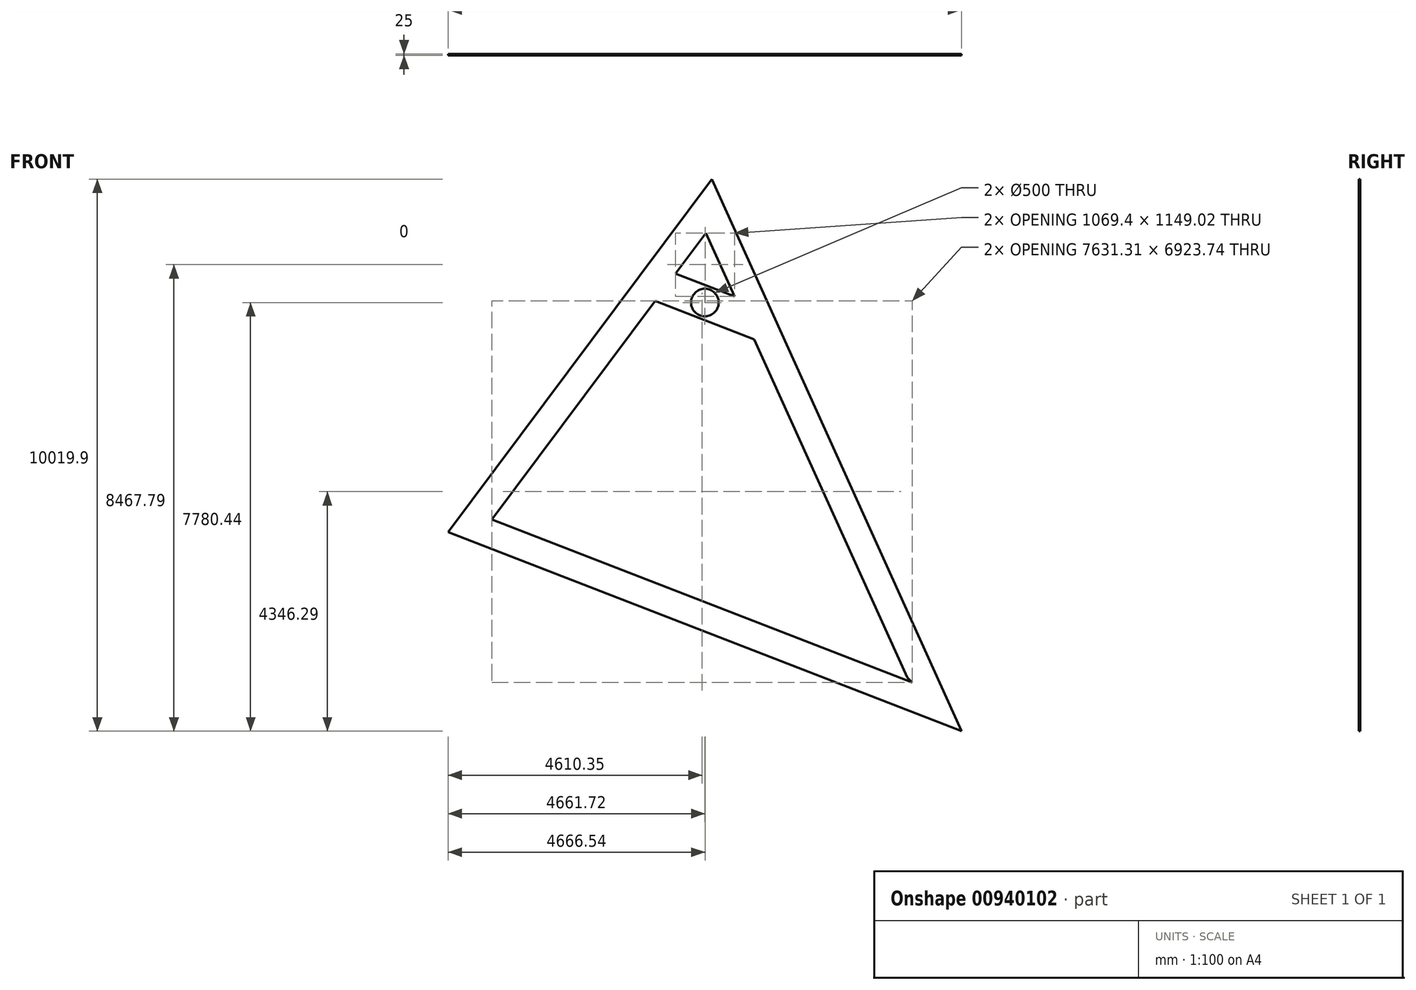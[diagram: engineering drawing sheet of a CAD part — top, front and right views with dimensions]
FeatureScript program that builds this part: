
annotation { "Feature Type Name" : "Feature", "Feature Type Description" : "" }
export const myFeature = defineFeature(function(context is Context, id is Id, definition is map)
    precondition{}
    {
        {
            var Q0;
            Q0=qCreatedBy(makeId("Front.planeOp"),FACE);
            var sketch = newSketch(context, id + "F0", { "sketchPlane" : qUnion([Q0])});
            skLineSegment(sketch, "E0", {"start": v(1258.9, -6409.87) * mm, "end": v(10584.54, -10019.94) * mm});
            skLineSegment(sketch, "E1", {"start": v(10584.54, -10019.94) * mm, "end": v(6045.72, 0) * mm});
            skLineSegment(sketch, "E2", {"start": v(6045.72, 0) * mm, "end": v(1258.9, -6409.87) * mm});
            skLineSegment(sketch, "E3", {"start": v(1258.9, -6409.87) * mm, "end": v(8315.13, -5009.97) * mm});
            skLineSegment(sketch, "E4", {"start": v(10584.54, -10019.94) * mm, "end": v(3652.31, -3204.93) * mm});
            skPoint(sketch, "E5", {"position": v(5963.05, -5476.6) * mm});
            skLineSegment(sketch, "E6", {"start": v(1743, -6597.27) * mm, "end": v(6281.33, -520.13) * mm});
            skLineSegment(sketch, "E7", {"start": v(5704.05, -457.51) * mm, "end": v(9918.91, -9762.26) * mm});
            skLineSegment(sketch, "E8", {"start": v(1569.5, -5993.95) * mm, "end": v(10290.02, -9369.77) * mm});
            skLineSegment(sketch, "E9", {"start": v(5390.74, -1712.68) * mm, "end": v(6460.14, -2126.66) * mm});
            skLineSegment(sketch, "E10", {"start": v(5018.02, -2211.78) * mm, "end": v(6813.56, -2906.86) * mm});
            skCircle(sketch, "E11", {"center": v(5920.62, -2239.5) * mm, "radius": 250 * mm});
            skPoint(sketch, "E12", {"position": v(5915.79, -2559.32) * mm});
            skPoint(sketch, "E13", {"position": v(5925.44, -1919.67) * mm});
            skLineSegment(sketch, "E14", {"start": v(5925.44, -1919.67) * mm, "end": v(5915.79, -2559.32) * mm});
            skSolve(sketch);
        }
        {
            var Q0;
            {var subQ1=sQuery(id+"F0.wireOp",EDGE,"E2");var subQ6=sQuery(id+"F0.wireOp",EDGE,"E4");var subQ9=makeQuery(id+"F0.imprint","INTERSECT",VERTEX,{"derivedFrom":[subQ1,subQ6]});Q0=makeQuery(id+"F0.imprint","IMPRINT",FACE,{"disambiguationData":[TD([[makeQuery(id+"F0.imprint","IMPRINT",EDGE,{"disambiguationData":[TD([[subQ9,1.0]])],"derivedFrom":subQ1}),1.0]])]});}
            var Q1;
            {var subQ0=sQuery(id+"F0.wireOp",EDGE,"fM5ZJTd4-uyG9-POUc-NQYo-ETeNcUDX0p3K");var subQ1=sQuery(id+"F0.wireOp",EDGE,"E6");var subQ2=makeQuery(id+"F0.imprint","INTERSECT",VERTEX,{"derivedFrom":[subQ1,subQ0]});Q1=makeQuery(id+"F0.imprint","IMPRINT",FACE,{"disambiguationData":[TD([[makeQuery(id+"F0.imprint","IMPRINT",EDGE,{"disambiguationData":[TD([[subQ2,-1.0]])],"derivedFrom":subQ1}),1.0]])]});}
            var Q2;
            {var subQ1=sQuery(id+"F0.wireOp",EDGE,"E2");var subQ3=sQuery(id+"F0.wireOp",EDGE,"E7");var subQ4=makeQuery(id+"F0.imprint","INTERSECT",VERTEX,{"derivedFrom":[subQ1,subQ3]});Q2=makeQuery(id+"F0.imprint","IMPRINT",FACE,{"disambiguationData":[TD([[makeQuery(id+"F0.imprint","IMPRINT",EDGE,{"disambiguationData":[TD([[subQ4,-1.0]])],"derivedFrom":subQ3}),1.0]])]});}
            var Q3;
            {var subQ1=sQuery(id+"F0.wireOp",EDGE,"c8Q3rwKz-DZUh-2BjS-u902-BvDDxR5sp2cA");var subQ3=sQuery(id+"F0.wireOp",EDGE,"E6");var subQ4=makeQuery(id+"F0.imprint","INTERSECT",VERTEX,{"derivedFrom":[subQ1,subQ3]});Q3=makeQuery(id+"F0.imprint","IMPRINT",FACE,{"disambiguationData":[TD([[makeQuery(id+"F0.imprint","IMPRINT",EDGE,{"disambiguationData":[TD([[subQ4,1.0]])],"derivedFrom":subQ3}),1.0]])]});}
            var Q4;
            {var subQ1=sQuery(id+"F0.wireOp",EDGE,"E1");var subQ3=sQuery(id+"F0.wireOp",EDGE,"E6");var subQ4=makeQuery(id+"F0.imprint","INTERSECT",VERTEX,{"derivedFrom":[subQ1,subQ3]});Q4=makeQuery(id+"F0.imprint","IMPRINT",FACE,{"disambiguationData":[TD([[makeQuery(id+"F0.imprint","IMPRINT",EDGE,{"disambiguationData":[TD([[subQ4,1.0]])],"derivedFrom":subQ3}),1.0]])]});}
            var Q5;
            {var subQ1=sQuery(id+"F0.wireOp",EDGE,"E1");var subQ7=sQuery(id+"F0.wireOp",EDGE,"E3");var subQ8=makeQuery(id+"F0.imprint","INTERSECT",VERTEX,{"derivedFrom":[subQ1,subQ7]});Q5=makeQuery(id+"F0.imprint","IMPRINT",FACE,{"disambiguationData":[TD([[makeQuery(id+"F0.imprint","IMPRINT",EDGE,{"disambiguationData":[TD([[subQ8,-1.0]])],"derivedFrom":subQ1}),1.0]])]});}
            var Q6;
            {var subQ0=sQuery(id+"F0.wireOp",EDGE,"E6");var subQ1=sQuery(id+"F0.wireOp",EDGE,"c8Q3rwKz-DZUh-2BjS-u902-BvDDxR5sp2cA");var subQ2=makeQuery(id+"F0.imprint","INTERSECT",VERTEX,{"derivedFrom":[subQ1,subQ0]});Q6=makeQuery(id+"F0.imprint","IMPRINT",FACE,{"disambiguationData":[TD([[makeQuery(id+"F0.imprint","IMPRINT",EDGE,{"disambiguationData":[TD([[subQ2,-1.0]])],"derivedFrom":subQ1}),-1.0]])]});}
            var Q7;
            {var subQ5=sQuery(id+"F0.wireOp",EDGE,"E3");var subQ6=sQuery(id+"F0.wireOp",EDGE,"E1");var subQ7=makeQuery(id+"F0.imprint","INTERSECT",VERTEX,{"derivedFrom":[subQ6,subQ5]});Q7=makeQuery(id+"F0.imprint","IMPRINT",FACE,{"disambiguationData":[TD([[makeQuery(id+"F0.imprint","IMPRINT",EDGE,{"disambiguationData":[TD([[subQ7,1.0]])],"derivedFrom":subQ6}),1.0]])]});}
            var Q8;
            {var subQ1=sQuery(id+"F0.wireOp",EDGE,"E1");var subQ3=sQuery(id+"F0.wireOp",EDGE,"E8");var subQ4=makeQuery(id+"F0.imprint","INTERSECT",VERTEX,{"derivedFrom":[subQ1,subQ3]});Q8=makeQuery(id+"F0.imprint","IMPRINT",FACE,{"disambiguationData":[TD([[makeQuery(id+"F0.imprint","IMPRINT",EDGE,{"disambiguationData":[TD([[subQ4,1.0]])],"derivedFrom":subQ3}),-1.0]])]});}
            var Q9;
            {var subQ1=sQuery(id+"F0.wireOp",EDGE,"E0");var subQ3=sQuery(id+"F0.wireOp",EDGE,"E7");var subQ4=makeQuery(id+"F0.imprint","INTERSECT",VERTEX,{"derivedFrom":[subQ1,subQ3]});Q9=makeQuery(id+"F0.imprint","IMPRINT",FACE,{"disambiguationData":[TD([[makeQuery(id+"F0.imprint","IMPRINT",EDGE,{"disambiguationData":[TD([[subQ4,1.0]])],"derivedFrom":subQ3}),1.0]])]});}
            var Q10;
            {var subQ0=sQuery(id+"F0.wireOp",EDGE,"c8Q3rwKz-DZUh-2BjS-u902-BvDDxR5sp2cA");var subQ1=sQuery(id+"F0.wireOp",EDGE,"E0");var subQ2=makeQuery(id+"F0.imprint","INTERSECT",VERTEX,{"derivedFrom":[subQ1,subQ0]});Q10=makeQuery(id+"F0.imprint","IMPRINT",FACE,{"disambiguationData":[TD([[makeQuery(id+"F0.imprint","IMPRINT",EDGE,{"disambiguationData":[TD([[subQ2,-1.0]])],"derivedFrom":subQ1}),1.0]])]});}
            var Q11;
            {var subQ0=sQuery(id+"F0.wireOp",EDGE,"c8Q3rwKz-DZUh-2BjS-u902-BvDDxR5sp2cA");var subQ1=sQuery(id+"F0.wireOp",EDGE,"E0");var subQ2=makeQuery(id+"F0.imprint","INTERSECT",VERTEX,{"derivedFrom":[subQ1,subQ0]});Q11=makeQuery(id+"F0.imprint","IMPRINT",FACE,{"disambiguationData":[TD([[makeQuery(id+"F0.imprint","IMPRINT",EDGE,{"disambiguationData":[TD([[subQ2,1.0]])],"derivedFrom":subQ1}),1.0]])]});}
            var Q12;
            {var subQ1=sQuery(id+"F0.wireOp",EDGE,"E0");var subQ3=sQuery(id+"F0.wireOp",EDGE,"E6");var subQ4=makeQuery(id+"F0.imprint","INTERSECT",VERTEX,{"derivedFrom":[subQ1,subQ3]});Q12=makeQuery(id+"F0.imprint","IMPRINT",FACE,{"disambiguationData":[TD([[makeQuery(id+"F0.imprint","IMPRINT",EDGE,{"disambiguationData":[TD([[subQ4,-1.0]])],"derivedFrom":subQ3}),1.0]])]});}
            var Q13;
            {var subQ0=sQuery(id+"F0.wireOp",EDGE,"E3");var subQ5=sQuery(id+"F0.wireOp",EDGE,"E6");var subQ6=makeQuery(id+"F0.imprint","INTERSECT",VERTEX,{"derivedFrom":[subQ0,subQ5]});Q13=makeQuery(id+"F0.imprint","IMPRINT",FACE,{"disambiguationData":[TD([[makeQuery(id+"F0.imprint","IMPRINT",EDGE,{"disambiguationData":[TD([[subQ6,-1.0]])],"derivedFrom":subQ5}),1.0]])]});}
            var Q14;
            {var subQ0=sQuery(id+"F0.wireOp",EDGE,"E4");var subQ1=sQuery(id+"F0.wireOp",EDGE,"E2");var subQ2=makeQuery(id+"F0.imprint","INTERSECT",VERTEX,{"derivedFrom":[subQ1,subQ0]});Q14=makeQuery(id+"F0.imprint","IMPRINT",FACE,{"disambiguationData":[TD([[makeQuery(id+"F0.imprint","IMPRINT",EDGE,{"disambiguationData":[TD([[subQ2,-1.0]])],"derivedFrom":subQ1}),1.0]])]});}
            var Q15;
            {var subQ0=sQuery(id+"F0.wireOp",EDGE,"E6");var subQ1=sQuery(id+"F0.wireOp",EDGE,"E0");var subQ2=makeQuery(id+"F0.imprint","INTERSECT",VERTEX,{"derivedFrom":[subQ1,subQ0]});Q15=makeQuery(id+"F0.imprint","IMPRINT",FACE,{"disambiguationData":[TD([[makeQuery(id+"F0.imprint","IMPRINT",EDGE,{"disambiguationData":[TD([[subQ2,-1.0]])],"derivedFrom":subQ1}),1.0]])]});}
            var Q16;
            {var subQ0=sQuery(id+"F0.wireOp",EDGE,"E6");var subQ1=sQuery(id+"F0.wireOp",EDGE,"E3");var subQ2=makeQuery(id+"F0.imprint","INTERSECT",VERTEX,{"derivedFrom":[subQ1,subQ0]});Q16=makeQuery(id+"F0.imprint","IMPRINT",FACE,{"disambiguationData":[TD([[makeQuery(id+"F0.imprint","IMPRINT",EDGE,{"disambiguationData":[TD([[subQ2,-1.0]])],"derivedFrom":subQ1}),1.0]])]});}
            var Q17;
            {var subQ0=sQuery(id+"F0.wireOp",EDGE,"E9");Q17=makeQuery(id+"F0.imprint","IMPRINT",FACE,{"disambiguationData":[TD([[makeQuery(id+"F0.imprint","IMPRINT",EDGE,{"derivedFrom":subQ0}),-1.0]])]});}
            extrude(context, id + "F1", {"entities" : qUnion([Q0, Q1, Q2, Q3, Q4, Q5, Q6, Q7, Q8, Q9, Q10, Q11, Q12, Q13, Q14, Q15, Q16, Q17]), "depth" : 25 * mm, "offsetDistance" : 25 * mm});
        }
    });
